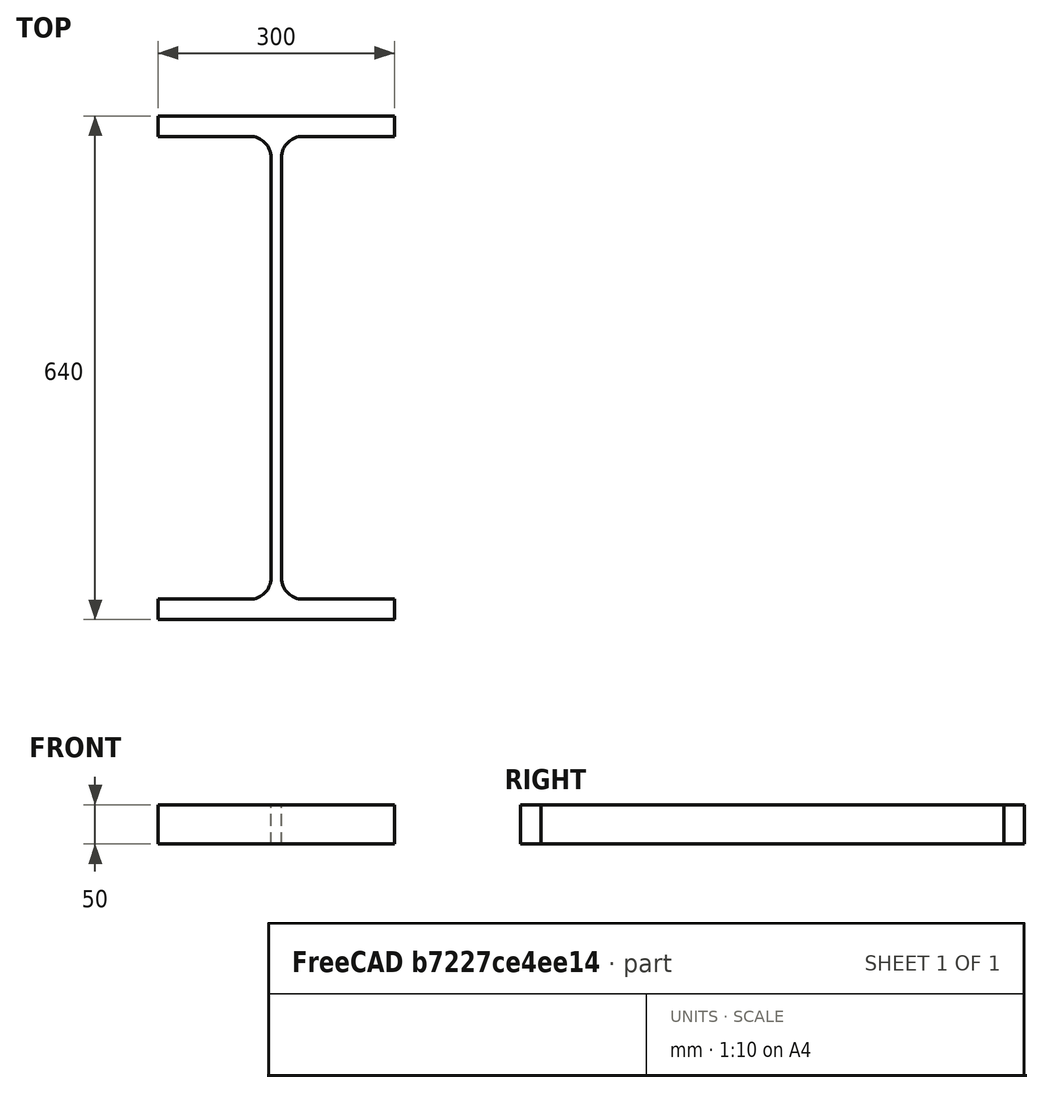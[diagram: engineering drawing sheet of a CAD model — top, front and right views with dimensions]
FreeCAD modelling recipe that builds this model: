
FCSTD DOCUMENT  (FreeCAD 0.15R4671 (Git))
Label: HE-A-Profile 650 DIN1025-3 S235JR
License: All rights reserved
LicenseURL: http://en.wikipedia.org/wiki/All_rights_reserved
objects: Sketcher::SketchObject×1, Part::Extrusion×1
note: 2 computed .brp shape members not serialized (recipe doc carries the construction recipe); baked Part::Feature solids carry a one-line shape summary decoded from their .brp

FEATURE [Sketcher::SketchObject] Sketch
  sketch-geometry (16):
    g0: LineSegment StartX=6.75 StartY=-267 StartZ=0 EndX=6.75 EndY=267 EndZ=0
    g1: LineSegment StartX=33.75 StartY=294 StartZ=0 EndX=150 EndY=294 EndZ=0
    g2: LineSegment StartX=150 StartY=294 StartZ=0 EndX=150 EndY=320 EndZ=0
    g3: LineSegment StartX=150 StartY=320 StartZ=0 EndX=-150 EndY=320 EndZ=0
    g4: LineSegment StartX=-150 StartY=320 StartZ=0 EndX=-150 EndY=294 EndZ=0
    g5: LineSegment StartX=-150 StartY=294 StartZ=0 EndX=-33.75 EndY=294 EndZ=0
    g6: LineSegment StartX=-6.75 StartY=267 StartZ=0 EndX=-6.75 EndY=-267 EndZ=0
    g7: LineSegment StartX=-33.75 StartY=-294 StartZ=0 EndX=-150 EndY=-294 EndZ=0
    g8: LineSegment StartX=-150 StartY=-294 StartZ=0 EndX=-150 EndY=-320 EndZ=0
    g9: LineSegment StartX=-150 StartY=-320 StartZ=0 EndX=150 EndY=-320 EndZ=0
    g10: LineSegment StartX=150 StartY=-320 StartZ=0 EndX=150 EndY=-294 EndZ=0
    g11: LineSegment StartX=150 StartY=-294 StartZ=0 EndX=33.75 EndY=-294 EndZ=0
    g12: ArcOfCircle CenterX=33.75 CenterY=267 CenterZ=0 NormalX=0 NormalY=0 NormalZ=1 Radius=27 StartAngle=1.5708 EndAngle=3.14159
    g13: ArcOfCircle CenterX=33.75 CenterY=-267 CenterZ=0 NormalX=0 NormalY=0 NormalZ=1 Radius=27 StartAngle=3.14159 EndAngle=4.71239
    g14: ArcOfCircle CenterX=-33.75 CenterY=267 CenterZ=0 NormalX=0 NormalY=0 NormalZ=1 Radius=27 StartAngle=0 EndAngle=1.5708
    g15: ArcOfCircle CenterX=-33.75 CenterY=-267 CenterZ=0 NormalX=0 NormalY=0 NormalZ=1 Radius=27 StartAngle=4.71239 EndAngle=6.28319
  constraints (42):
    c: Vertical(g0)
    c: Coincident(g2,g1)
    c: Vertical(g2)
    c: Coincident(g3,g2)
    c: Coincident(g4,g3)
    c: Vertical(g4)
    c: Coincident(g5,g4)
    c: Horizontal(g5)
    c: Vertical(g6)
    c: Horizontal(g7)
    c: Coincident(g8,g7)
    c: Vertical(g8)
    c: Coincident(g9,g8)
    c: Horizontal(g9)
    c: Coincident(g10,g9)
    c: Vertical(g10)
    c: Coincident(g11,g10)
    c: Horizontal(g11)
    c: Tangent(g1,g12) = 1.5708
    c: Tangent(g0,g12) = 1.5708
    c: Tangent(g0,g13) = 1.5708
    c: Tangent(g11,g13) = 1.5708
    c: Tangent(g5,g14) = 1.5708
    c: Tangent(g6,g14) = 1.5708
    c: Tangent(g6,g15) = 1.5708
    c: Tangent(g7,g15) = 1.5708
    c: Equal(g3,g9)
    c: Equal(g2,g4)
    c: Equal(g4,g8)
    c: Equal(g8,g10)
    c: Equal(g12,g14)
    c: Equal(g14,g15)
    c: Equal(g15,g13)
    c: Symmetric(g2,g3,g-2)
    c: Symmetric(g9,g8,g-2)
    c: Symmetric(g0,g6,g-2)
    c: Symmetric(g2,g9,g-1)
    c: DistanceY(g2,g9) = -640
    c: DistanceX(g3) = -300
    c: DistanceX(g0,g6) = -13.5
    c: DistanceY(g2) = 26
    c: Radius(g12) = 27
FEATURE [Part::Extrusion] Extrude  label="HE-A-Profile 650 DIN1025-3 S235JR"
  Base = -> Sketch
  Dir = (0,0,50)
  Solid = true
